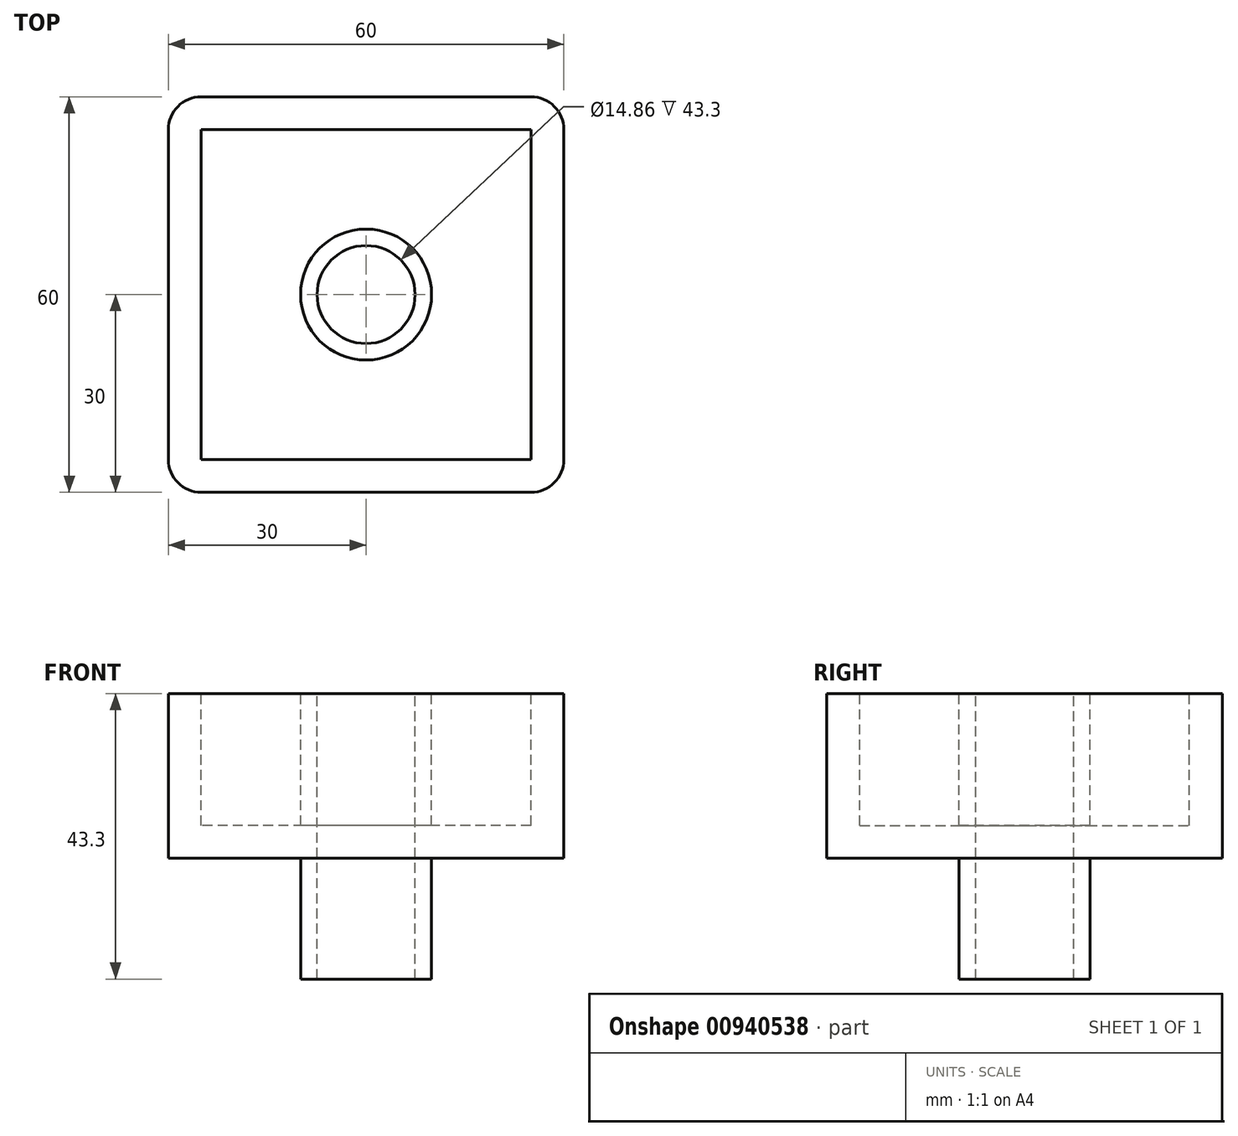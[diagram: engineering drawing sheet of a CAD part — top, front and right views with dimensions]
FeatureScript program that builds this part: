
annotation { "Feature Type Name" : "Feature", "Feature Type Description" : "" }
export const myFeature = defineFeature(function(context is Context, id is Id, definition is map)
    precondition{}
    {
        {
            var Q0;
            Q0=qCreatedBy(makeId("Top.planeOp"),FACE);
            var sketch = newSketch(context, id + "F0", { "sketchPlane" : qUnion([Q0])});
            skLineSegment(sketch, "E0.bottom", {"start": v(30, -30) * mm, "end": v(-30, -30) * mm});
            skLineSegment(sketch, "E0.top", {"start": v(30, 30) * mm, "end": v(-30, 30) * mm});
            skLineSegment(sketch, "E0.left", {"start": v(30, -30) * mm, "end": v(30, 30) * mm});
            skLineSegment(sketch, "E0.right", {"start": v(-30, -30) * mm, "end": v(-30, 30) * mm});
            skPoint(sketch, "E0.middle", {"position": v(0, 0) * mm});
            skSolve(sketch);
        }
        {
            var Q0;
            Q0=makeQuery(id+"F0.imprint","IMPRINT",FACE,{"disambiguationData":[TD([[makeQuery(id+"F0.imprint","IMPRINT",EDGE,{"derivedFrom":sQuery(id+"F0.wireOp",EDGE,"E0.bottom")}),-1.0]])]});
            extrude(context, id + "F1", {"entities" : qUnion([Q0]), "depth" : 25 * mm, "offsetDistance" : 25 * mm});
        }
        {
            var Q0;
            Q0=makeQuery(id+"F1.opExtrude","CAP_FACE",FACE,{"disambiguationData":[OSD([sQuery(id+"F0.wireOp",EDGE,"E0.bottom"),sQuery(id+"F0.wireOp",EDGE,"E0.top"),sQuery(id+"F0.wireOp",EDGE,"E0.left"),sQuery(id+"F0.wireOp",EDGE,"E0.right")])],"isStart":false});
            var sketch = newSketch(context, id + "F2", { "sketchPlane" : qUnion([Q0])});
            skLineSegment(sketch, "E1.bottom", {"start": v(25, -25) * mm, "end": v(-25, -25) * mm});
            skLineSegment(sketch, "E1.top", {"start": v(25, 25) * mm, "end": v(-25, 25) * mm});
            skLineSegment(sketch, "E1.left", {"start": v(25, -25) * mm, "end": v(25, 25) * mm});
            skLineSegment(sketch, "E1.right", {"start": v(-25, -25) * mm, "end": v(-25, 25) * mm});
            skPoint(sketch, "E1.middle", {"position": v(0, 0) * mm});
            skSolve(sketch);
        }
        {
            var Q0;
            Q0 = qSketchRegion(id + "F2", true);
            extrude(context, id + "F3", {"entities" : qUnion([Q0]), "operationType" : NewBodyOperationType.REMOVE, "oppositeDirection" : true, "depth" : 20 * mm, "offsetDistance" : 25 * mm});
        }
        {
            var Q0;
            Q0=makeQuery(id+"F1.opExtrude","CAP_FACE",FACE,{"disambiguationData":[OSD([sQuery(id+"F0.wireOp",EDGE,"E0.bottom"),sQuery(id+"F0.wireOp",EDGE,"E0.top"),sQuery(id+"F0.wireOp",EDGE,"E0.left"),sQuery(id+"F0.wireOp",EDGE,"E0.right")])],"isStart":false});
            var sketch = newSketch(context, id + "F4", { "sketchPlane" : qUnion([Q0])});
            skCircle(sketch, "E2", {"center": v(0, 0) * mm, "radius": 7.43 * mm});
            skCircle(sketch, "E3", {"center": v(0, 0) * mm, "radius": 9.93 * mm});
            skSolve(sketch);
        }
        {
            var Q0;
            Q0 = qSketchRegion(id + "F4", true);
            extrude(context, id + "F5", {"entities" : qUnion([Q0]), "operationType" : NewBodyOperationType.ADD, "oppositeDirection" : true, "depth" : 43.3 * mm, "offsetDistance" : 25 * mm});
        }
        {
            var Q0;
            Q0=makeQuery(id+"F5.opExtrude","CAP_FACE",FACE,{"disambiguationData":[OSD([sQuery(id+"F4.wireOp",EDGE,"E2"),sQuery(id+"F4.wireOp",EDGE,"E3")])],"isStart":true});
            var sketch = newSketch(context, id + "F6", { "sketchPlane" : qUnion([Q0])});
            skCircle(sketch, "E4", {"center": v(0, 0) * mm, "radius": 7.43 * mm});
            skSolve(sketch);
        }
        {
            var Q0;
            Q0 = qSketchRegion(id + "F6", true);
            extrude(context, id + "F7", {"entities" : qUnion([Q0]), "operationType" : NewBodyOperationType.REMOVE, "oppositeDirection" : true, "depth" : 56.5 * mm, "offsetDistance" : 25 * mm});
        }
        {
            var Q0;
            Q0=makeQuery(id+"F1.opExtrude","SWEPT_EDGE",EDGE,{"disambiguationData":[OSD([sQuery(id+"F0.wireOp",EDGE,"E0.bottom"),sQuery(id+"F0.wireOp",EDGE,"E0.right")])]});
            var Q1;
            Q1=makeQuery(id+"F1.opExtrude","SWEPT_EDGE",EDGE,{"disambiguationData":[OSD([sQuery(id+"F0.wireOp",EDGE,"E0.bottom"),sQuery(id+"F0.wireOp",EDGE,"E0.left")])]});
            var Q2;
            Q2=makeQuery(id+"F1.opExtrude","SWEPT_EDGE",EDGE,{"disambiguationData":[OSD([sQuery(id+"F0.wireOp",EDGE,"E0.top"),sQuery(id+"F0.wireOp",EDGE,"E0.left")])]});
            var Q3;
            Q3=makeQuery(id+"F1.opExtrude","SWEPT_EDGE",EDGE,{"disambiguationData":[OSD([sQuery(id+"F0.wireOp",EDGE,"E0.top"),sQuery(id+"F0.wireOp",EDGE,"E0.right")])]});
            fillet(context, id + "F8", {"entities" : qUnion([Q0, Q1, Q2, Q3]), "radius" : 5 * mm, "tangentPropagation" : true, "allowEdgeOverflow" : false});
        }
    });
